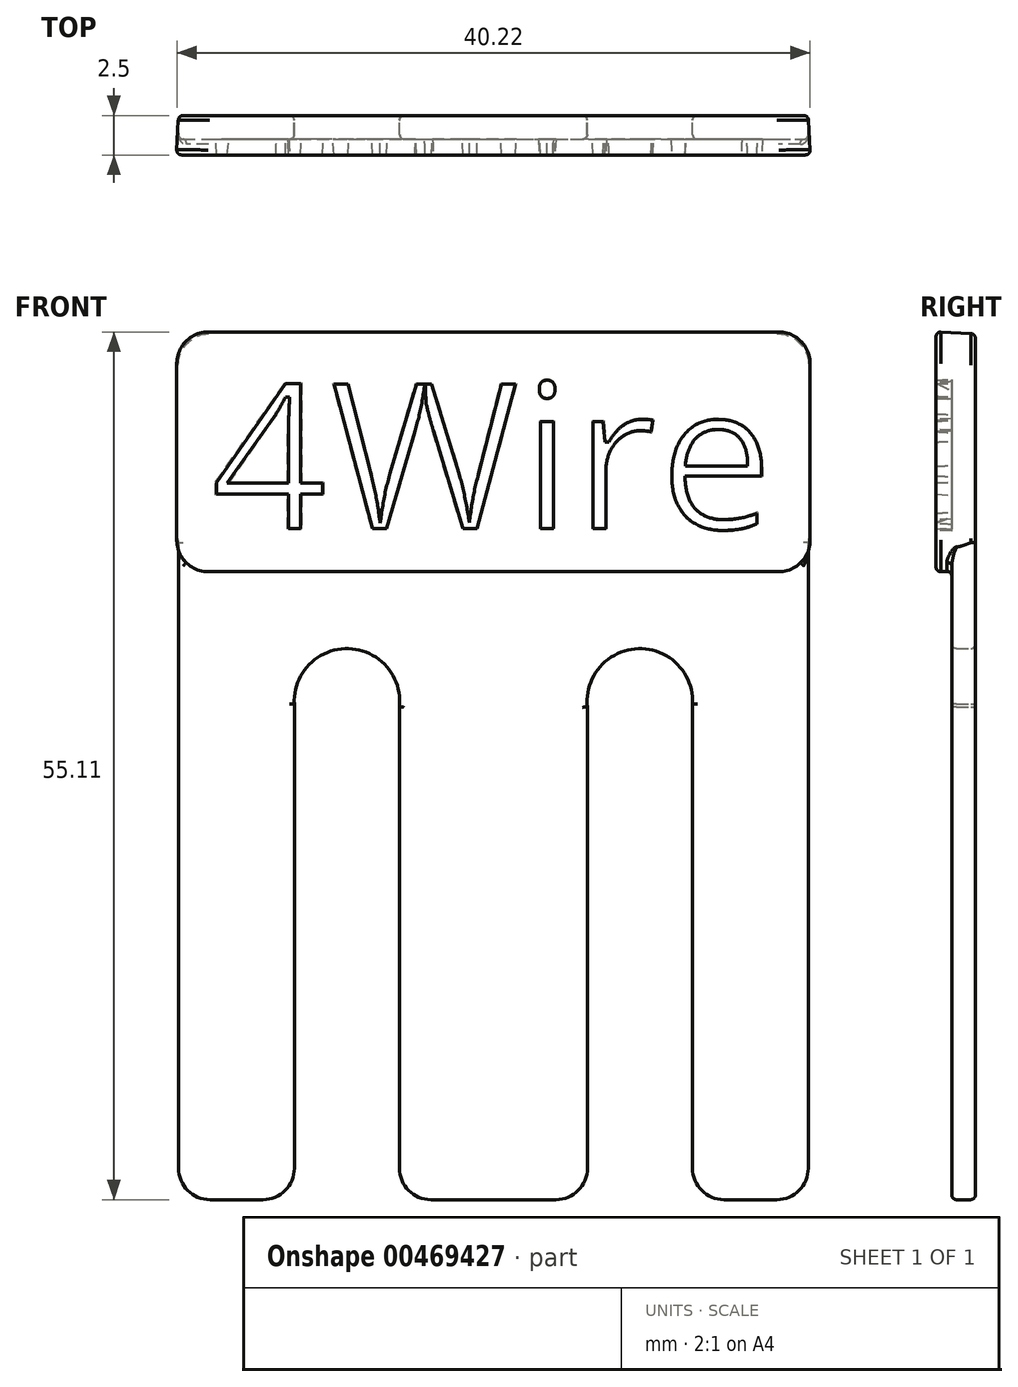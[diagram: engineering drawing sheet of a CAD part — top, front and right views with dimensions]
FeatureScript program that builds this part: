
annotation { "Feature Type Name" : "Feature", "Feature Type Description" : "" }
export const myFeature = defineFeature(function(context is Context, id is Id, definition is map)
    precondition{}
    {
        {
            var Q0;
            Q0=qCreatedBy(makeId("Front.planeOp"),FACE);
            var sketch = newSketch(context, id + "F0", { "sketchPlane" : qUnion([Q0])});
            skLineSegment(sketch, "E0.bottom", {"start": v(-20, 27.5) * mm, "end": v(20, 27.5) * mm});
            skLineSegment(sketch, "E0.top", {"start": v(-20, -27.5) * mm, "end": v(20, -27.5) * mm});
            skLineSegment(sketch, "E0.left", {"start": v(-20, 27.5) * mm, "end": v(-20, -27.5) * mm});
            skLineSegment(sketch, "E0.right", {"start": v(20, 27.5) * mm, "end": v(20, -27.5) * mm});
            skPoint(sketch, "E0.middle", {"position": v(0, 0) * mm});
            skLineSegment(sketch, "E1.top", {"start": v(-20, 12.5) * mm, "end": v(20, 12.5) * mm});
            skLineSegment(sketch, "E1.left", {"start": v(-20, 27.5) * mm, "end": v(-20, 12.5) * mm});
            skLineSegment(sketch, "E1.right", {"start": v(20, 27.5) * mm, "end": v(20, 12.5) * mm});
            skCircle(sketch, "E2", {"center": v(-9.3, 4.15) * mm, "radius": 3.35 * mm});
            skLineSegment(sketch, "E3", {"start": v(-12.65, 4.32) * mm, "end": v(-12.65, -27.5) * mm});
            skLineSegment(sketch, "E4", {"start": v(-5.97, 3.8) * mm, "end": v(-5.97, -27.5) * mm});
            skCircle(sketch, "E5.MirrorC", {"center": v(9.3, 4.15) * mm, "radius": 3.35 * mm});
            skLineSegment(sketch, "E6.MirrorCS", {"start": v(12.65, 4.32) * mm, "end": v(12.65, -27.5) * mm});
            skLineSegment(sketch, "E7.MirrorCS", {"start": v(5.97, 3.8) * mm, "end": v(5.97, -27.5) * mm});
            skText(sketch, "E8", { "text": "4Wire", "fontName": "OpenSans-Regular.ttf"});
            const initialGuessF0  = {"E8": [-0.018, 0.01501, 1, 0, 0.00949]};
            skSetInitialGuess(sketch, initialGuessF0);
            skSolve(sketch);
        }
        {
            var Q0;
            {var subQ5=sQuery(id+"F0.wireOp",EDGE,"E0.left");Q0=makeQuery(id+"F0.imprint","IMPRINT",FACE,{"disambiguationData":[TD([[makeQuery(id+"F0.imprint","IMPRINT",EDGE,{"derivedFrom":subQ5}),1.0]])]});}
            var Q1;
            Q1=makeQuery(id+"F0.imprint","IMPRINT",FACE,{"disambiguationData":[TD([[makeQuery(id+"F0.imprint","IMPRINT",EDGE,{"derivedFrom":sQuery(id+"F0.wireOp",EDGE,"E8.sketch_text.stroke-62")}),-1.0]])]});
            var Q2;
            Q2=makeQuery(id+"F0.imprint","IMPRINT",FACE,{"disambiguationData":[TD([[makeQuery(id+"F0.imprint","IMPRINT",EDGE,{"derivedFrom":sQuery(id+"F0.wireOp",EDGE,"E8.sketch_text.stroke-49")}),-1.0]])]});
            var Q3;
            Q3=makeQuery(id+"F0.imprint","IMPRINT",FACE,{"disambiguationData":[TD([[makeQuery(id+"F0.imprint","IMPRINT",EDGE,{"derivedFrom":sQuery(id+"F0.wireOp",EDGE,"E8.sketch_text.stroke-37")}),-1.0]])]});
            var Q4;
            Q4=makeQuery(id+"F0.imprint","IMPRINT",FACE,{"disambiguationData":[TD([[makeQuery(id+"F0.imprint","IMPRINT",EDGE,{"derivedFrom":sQuery(id+"F0.wireOp",EDGE,"E8.sketch_text.stroke-41")}),-1.0]])]});
            var Q5;
            Q5=makeQuery(id+"F0.imprint","IMPRINT",FACE,{"disambiguationData":[TD([[makeQuery(id+"F0.imprint","IMPRINT",EDGE,{"derivedFrom":sQuery(id+"F0.wireOp",EDGE,"E8.sketch_text.stroke-17")}),-1.0]])]});
            var Q6;
            Q6=makeQuery(id+"F0.imprint","IMPRINT",FACE,{"disambiguationData":[TD([[makeQuery(id+"F0.imprint","IMPRINT",EDGE,{"derivedFrom":sQuery(id+"F0.wireOp",EDGE,"E8.sketch_text.stroke-0")}),-1.0]])]});
            extrude(context, id + "F1", {"entities" : qUnion([Q0, Q1, Q2, Q3, Q4, Q5, Q6]), "depth" : 1.5 * mm});
        }
        {
            var Q0;
            Q0=makeQuery(id+"F0.imprint","IMPRINT",FACE,{"disambiguationData":[TD([[makeQuery(id+"F0.imprint","IMPRINT",EDGE,{"derivedFrom":sQuery(id+"F0.wireOp",EDGE,"E0.bottom")}),-1.0]])]});
            var Q1;
            Q1=makeQuery(id+"F0.imprint","IMPRINT",FACE,{"disambiguationData":[TD([[makeQuery(id+"F0.imprint","IMPRINT",EDGE,{"derivedFrom":sQuery(id+"F0.wireOp",EDGE,"E8.sketch_text.stroke-11")}),1.0]])]});
            var Q2;
            Q2=makeQuery(id+"F0.imprint","IMPRINT",FACE,{"disambiguationData":[TD([[makeQuery(id+"F0.imprint","IMPRINT",EDGE,{"derivedFrom":sQuery(id+"F0.wireOp",EDGE,"E8.sketch_text.stroke-76")}),1.0]])]});
            extrude(context, id + "F2", {"entities" : qUnion([Q0, Q1, Q2]), "operationType" : NewBodyOperationType.ADD, "depth" : 2.5 * mm, "hasDraft" : true, "draftAngle" : 3 * degree});
        }
        {
            var Q0;
            Q0=makeQuery(id+"F2.opExtrude","SWEPT_EDGE",EDGE,{"disambiguationData":[OSD([sQuery(id+"F0.wireOp",EDGE,"E0.bottom"),sQuery(id+"F0.wireOp",EDGE,"E1.right")])]});
            var Q1;
            Q1=makeQuery(id+"F2.opExtrude","SWEPT_EDGE",EDGE,{"disambiguationData":[OSD([sQuery(id+"F0.wireOp",EDGE,"E0.bottom"),sQuery(id+"F0.wireOp",EDGE,"E1.left")])]});
            var Q2;
            Q2=makeQuery(id+"F1.opExtrude","SWEPT_EDGE",EDGE,{"disambiguationData":[OSD([sQuery(id+"F0.wireOp",EDGE,"E0.top"),sQuery(id+"F0.wireOp",EDGE,"E3")])]});
            var Q3;
            Q3=makeQuery(id+"F1.opExtrude","SWEPT_EDGE",EDGE,{"disambiguationData":[OSD([sQuery(id+"F0.wireOp",EDGE,"E0.top"),sQuery(id+"F0.wireOp",EDGE,"E4")])]});
            var Q4;
            Q4=makeQuery(id+"F1.opExtrude","SWEPT_EDGE",EDGE,{"disambiguationData":[OSD([sQuery(id+"F0.wireOp",EDGE,"E0.top"),sQuery(id+"F0.wireOp",EDGE,"E7.MirrorCS")])]});
            var Q5;
            Q5=makeQuery(id+"F1.opExtrude","SWEPT_EDGE",EDGE,{"disambiguationData":[OSD([sQuery(id+"F0.wireOp",EDGE,"E0.top"),sQuery(id+"F0.wireOp",EDGE,"E6.MirrorCS")])]});
            var Q6;
            Q6=makeQuery(id+"F1.opExtrude","SWEPT_EDGE",EDGE,{"disambiguationData":[OSD([sQuery(id+"F0.wireOp",EDGE,"E0.top"),sQuery(id+"F0.wireOp",EDGE,"E0.right")])]});
            var Q7;
            Q7=makeQuery(id+"F1.opExtrude","SWEPT_EDGE",EDGE,{"disambiguationData":[OSD([sQuery(id+"F0.wireOp",EDGE,"E0.top"),sQuery(id+"F0.wireOp",EDGE,"E0.left")])]});
            var Q8;
            Q8=makeQuery(id+"F2.opExtrude","SWEPT_EDGE",EDGE,{"disambiguationData":[OSD([sQuery(id+"F0.wireOp",EDGE,"E0.right"),sQuery(id+"F0.wireOp",EDGE,"E1.top"),sQuery(id+"F0.wireOp",EDGE,"E1.right")])]});
            var Q9;
            Q9=makeQuery(id+"F2.opExtrude","SWEPT_EDGE",EDGE,{"disambiguationData":[OSD([sQuery(id+"F0.wireOp",EDGE,"E0.left"),sQuery(id+"F0.wireOp",EDGE,"E1.top"),sQuery(id+"F0.wireOp",EDGE,"E1.left")])]});
            fillet(context, id + "F3", {"entities" : qUnion([Q0, Q1, Q2, Q3, Q4, Q5, Q6, Q7, Q8, Q9]), "radius" : 2 * mm, "tangentPropagation" : true, "allowEdgeOverflow" : false});
        }
        {
            var Q0;
            Q0=makeQuery(id+"F2.opExtrude","CAP_EDGE",EDGE,{"disambiguationData":[OSD([sQuery(id+"F0.wireOp",EDGE,"E1.top")])],"isStart":false});
            var Q1;
            Q1=makeQuery(id+"F1.opExtrude","CAP_FACE",FACE,{"disambiguationData":[OSD([sQuery(id+"F0.wireOp",EDGE,"E0.top"),sQuery(id+"F0.wireOp",EDGE,"E0.left"),sQuery(id+"F0.wireOp",EDGE,"E0.right"),sQuery(id+"F0.wireOp",EDGE,"E1.top"),sQuery(id+"F0.wireOp",EDGE,"E2"),sQuery(id+"F0.wireOp",EDGE,"E3"),sQuery(id+"F0.wireOp",EDGE,"E4"),sQuery(id+"F0.wireOp",EDGE,"E5.MirrorC"),sQuery(id+"F0.wireOp",EDGE,"E6.MirrorCS"),sQuery(id+"F0.wireOp",EDGE,"E7.MirrorCS")])],"isStart":false});
            var Q2;
            {var subQ0=sQuery(id+"F0.wireOp",EDGE,"E8.sketch_text.stroke-80");var subQ1=sQuery(id+"F0.wireOp",EDGE,"E8.sketch_text.stroke-79");var subQ2=sQuery(id+"F0.wireOp",EDGE,"E8.sketch_text.stroke-78");var subQ3=sQuery(id+"F0.wireOp",EDGE,"E8.sketch_text.stroke-77");var subQ4=sQuery(id+"F0.wireOp",EDGE,"E8.sketch_text.stroke-76");var subQ5=sQuery(id+"F0.wireOp",EDGE,"E8.sketch_text.stroke-16");var subQ6=sQuery(id+"F0.wireOp",EDGE,"E8.sketch_text.stroke-15");var subQ7=sQuery(id+"F0.wireOp",EDGE,"E8.sketch_text.stroke-14");var subQ8=sQuery(id+"F0.wireOp",EDGE,"E8.sketch_text.stroke-13");var subQ9=sQuery(id+"F0.wireOp",EDGE,"E8.sketch_text.stroke-12");var subQ10=sQuery(id+"F0.wireOp",EDGE,"E8.sketch_text.stroke-11");var subQ11=sQuery(id+"F0.wireOp",EDGE,"E8.sketch_text.stroke-75");var subQ12=sQuery(id+"F0.wireOp",EDGE,"E8.sketch_text.stroke-74");var subQ13=sQuery(id+"F0.wireOp",EDGE,"E8.sketch_text.stroke-73");var subQ14=sQuery(id+"F0.wireOp",EDGE,"E8.sketch_text.stroke-72");var subQ15=sQuery(id+"F0.wireOp",EDGE,"E8.sketch_text.stroke-71");var subQ16=sQuery(id+"F0.wireOp",EDGE,"E8.sketch_text.stroke-70");var subQ17=sQuery(id+"F0.wireOp",EDGE,"E8.sketch_text.stroke-69");var subQ18=sQuery(id+"F0.wireOp",EDGE,"E8.sketch_text.stroke-68");var subQ19=sQuery(id+"F0.wireOp",EDGE,"E8.sketch_text.stroke-67");var subQ20=sQuery(id+"F0.wireOp",EDGE,"E8.sketch_text.stroke-66");var subQ21=sQuery(id+"F0.wireOp",EDGE,"E8.sketch_text.stroke-65");var subQ22=sQuery(id+"F0.wireOp",EDGE,"E8.sketch_text.stroke-64");var subQ23=sQuery(id+"F0.wireOp",EDGE,"E8.sketch_text.stroke-63");var subQ24=sQuery(id+"F0.wireOp",EDGE,"E8.sketch_text.stroke-62");var subQ25=sQuery(id+"F0.wireOp",EDGE,"E8.sketch_text.stroke-61");var subQ26=sQuery(id+"F0.wireOp",EDGE,"E8.sketch_text.stroke-60");var subQ27=sQuery(id+"F0.wireOp",EDGE,"E8.sketch_text.stroke-59");var subQ28=sQuery(id+"F0.wireOp",EDGE,"E8.sketch_text.stroke-58");var subQ29=sQuery(id+"F0.wireOp",EDGE,"E8.sketch_text.stroke-57");var subQ30=sQuery(id+"F0.wireOp",EDGE,"E8.sketch_text.stroke-56");var subQ31=sQuery(id+"F0.wireOp",EDGE,"E8.sketch_text.stroke-55");var subQ32=sQuery(id+"F0.wireOp",EDGE,"E8.sketch_text.stroke-54");var subQ33=sQuery(id+"F0.wireOp",EDGE,"E8.sketch_text.stroke-53");var subQ34=sQuery(id+"F0.wireOp",EDGE,"E8.sketch_text.stroke-52");var subQ35=sQuery(id+"F0.wireOp",EDGE,"E8.sketch_text.stroke-51");var subQ36=sQuery(id+"F0.wireOp",EDGE,"E8.sketch_text.stroke-50");var subQ37=sQuery(id+"F0.wireOp",EDGE,"E8.sketch_text.stroke-49");var subQ38=sQuery(id+"F0.wireOp",EDGE,"E8.sketch_text.stroke-48");var subQ39=sQuery(id+"F0.wireOp",EDGE,"E8.sketch_text.stroke-47");var subQ40=sQuery(id+"F0.wireOp",EDGE,"E8.sketch_text.stroke-46");var subQ41=sQuery(id+"F0.wireOp",EDGE,"E8.sketch_text.stroke-45");var subQ42=sQuery(id+"F0.wireOp",EDGE,"E8.sketch_text.stroke-44");var subQ43=sQuery(id+"F0.wireOp",EDGE,"E8.sketch_text.stroke-43");var subQ44=sQuery(id+"F0.wireOp",EDGE,"E8.sketch_text.stroke-42");var subQ45=sQuery(id+"F0.wireOp",EDGE,"E8.sketch_text.stroke-41");var subQ46=sQuery(id+"F0.wireOp",EDGE,"E8.sketch_text.stroke-40");var subQ47=sQuery(id+"F0.wireOp",EDGE,"E8.sketch_text.stroke-39");var subQ48=sQuery(id+"F0.wireOp",EDGE,"E8.sketch_text.stroke-38");var subQ49=sQuery(id+"F0.wireOp",EDGE,"E8.sketch_text.stroke-37");var subQ50=sQuery(id+"F0.wireOp",EDGE,"E8.sketch_text.stroke-36");var subQ51=sQuery(id+"F0.wireOp",EDGE,"E8.sketch_text.stroke-35");var subQ52=sQuery(id+"F0.wireOp",EDGE,"E8.sketch_text.stroke-34");var subQ53=sQuery(id+"F0.wireOp",EDGE,"E8.sketch_text.stroke-33");var subQ54=sQuery(id+"F0.wireOp",EDGE,"E8.sketch_text.stroke-32");var subQ55=sQuery(id+"F0.wireOp",EDGE,"E8.sketch_text.stroke-31");var subQ56=sQuery(id+"F0.wireOp",EDGE,"E8.sketch_text.stroke-30");var subQ57=sQuery(id+"F0.wireOp",EDGE,"E8.sketch_text.stroke-29");var subQ58=sQuery(id+"F0.wireOp",EDGE,"E8.sketch_text.stroke-28");var subQ59=sQuery(id+"F0.wireOp",EDGE,"E8.sketch_text.stroke-27");var subQ60=sQuery(id+"F0.wireOp",EDGE,"E8.sketch_text.stroke-26");var subQ61=sQuery(id+"F0.wireOp",EDGE,"E8.sketch_text.stroke-25");var subQ62=sQuery(id+"F0.wireOp",EDGE,"E8.sketch_text.stroke-24");var subQ63=sQuery(id+"F0.wireOp",EDGE,"E8.sketch_text.stroke-23");var subQ64=sQuery(id+"F0.wireOp",EDGE,"E8.sketch_text.stroke-22");var subQ65=sQuery(id+"F0.wireOp",EDGE,"E8.sketch_text.stroke-21");var subQ66=sQuery(id+"F0.wireOp",EDGE,"E8.sketch_text.stroke-20");var subQ67=sQuery(id+"F0.wireOp",EDGE,"E8.sketch_text.stroke-19");var subQ68=sQuery(id+"F0.wireOp",EDGE,"E8.sketch_text.stroke-18");var subQ69=sQuery(id+"F0.wireOp",EDGE,"E8.sketch_text.stroke-17");var subQ70=sQuery(id+"F0.wireOp",EDGE,"E8.sketch_text.stroke-10");var subQ71=sQuery(id+"F0.wireOp",EDGE,"E8.sketch_text.stroke-9");var subQ72=sQuery(id+"F0.wireOp",EDGE,"E8.sketch_text.stroke-8");var subQ73=sQuery(id+"F0.wireOp",EDGE,"E8.sketch_text.stroke-7");var subQ74=sQuery(id+"F0.wireOp",EDGE,"E8.sketch_text.stroke-6");var subQ75=sQuery(id+"F0.wireOp",EDGE,"E8.sketch_text.stroke-5");var subQ76=sQuery(id+"F0.wireOp",EDGE,"E8.sketch_text.stroke-4");var subQ77=sQuery(id+"F0.wireOp",EDGE,"E8.sketch_text.stroke-3");var subQ78=sQuery(id+"F0.wireOp",EDGE,"E8.sketch_text.stroke-2");var subQ79=sQuery(id+"F0.wireOp",EDGE,"E8.sketch_text.stroke-1");var subQ80=sQuery(id+"F0.wireOp",EDGE,"E8.sketch_text.stroke-0");var subQ81=sQuery(id+"F0.wireOp",EDGE,"E1.top");Q2=makeQuery(id+"F2.boolean.opBoolean","MERGE",FACE,{"derivedFrom":[makeQuery(id+"F1.opExtrude","CAP_FACE",FACE,{"disambiguationData":[OSD([sQuery(id+"F0.wireOp",EDGE,"E0.top"),sQuery(id+"F0.wireOp",EDGE,"E0.left"),sQuery(id+"F0.wireOp",EDGE,"E0.right"),subQ81,sQuery(id+"F0.wireOp",EDGE,"E2"),sQuery(id+"F0.wireOp",EDGE,"E3"),sQuery(id+"F0.wireOp",EDGE,"E4"),sQuery(id+"F0.wireOp",EDGE,"E5.MirrorC"),sQuery(id+"F0.wireOp",EDGE,"E6.MirrorCS"),sQuery(id+"F0.wireOp",EDGE,"E7.MirrorCS")])],"isStart":true}),makeQuery(id+"F1.opExtrude","CAP_FACE",FACE,{"disambiguationData":[OSD([subQ80,subQ79,subQ78,subQ77,subQ76,subQ75,subQ74,subQ73,subQ72,subQ71,subQ70,subQ10,subQ9,subQ8,subQ7,subQ6,subQ5])],"isStart":true}),makeQuery(id+"F1.opExtrude","CAP_FACE",FACE,{"disambiguationData":[OSD([subQ69,subQ68,subQ67,subQ66,subQ65,subQ64,subQ63,subQ62,subQ61,subQ60,subQ59,subQ58,subQ57,subQ56,subQ55,subQ54,subQ53,subQ52,subQ51,subQ50])],"isStart":true}),makeQuery(id+"F1.opExtrude","CAP_FACE",FACE,{"disambiguationData":[OSD([subQ49,subQ48,subQ47,subQ46])],"isStart":true}),makeQuery(id+"F1.opExtrude","CAP_FACE",FACE,{"disambiguationData":[OSD([subQ45,subQ44,subQ43,subQ42,subQ41,subQ40,subQ39,subQ38])],"isStart":true}),makeQuery(id+"F1.opExtrude","CAP_FACE",FACE,{"disambiguationData":[OSD([subQ37,subQ36,subQ35,subQ34,subQ33,subQ32,subQ31,subQ30,subQ29,subQ28,subQ27,subQ26,subQ25])],"isStart":true}),makeQuery(id+"F1.opExtrude","CAP_FACE",FACE,{"disambiguationData":[OSD([subQ24,subQ23,subQ22,subQ21,subQ20,subQ19,subQ18,subQ17,subQ16,subQ15,subQ14,subQ13,subQ12,subQ11,subQ4,subQ3,subQ2,subQ1,subQ0])],"isStart":true}),makeQuery(id+"F2.opExtrude","CAP_FACE",FACE,{"disambiguationData":[OSD([sQuery(id+"F0.wireOp",EDGE,"E0.bottom"),subQ81,sQuery(id+"F0.wireOp",EDGE,"E1.left"),sQuery(id+"F0.wireOp",EDGE,"E1.right"),subQ80,subQ79,subQ78,subQ77,subQ76,subQ75,subQ74,subQ73,subQ72,subQ71,subQ70,subQ69,subQ68,subQ67,subQ66,subQ65,subQ64,subQ63,subQ62,subQ61,subQ60,subQ59,subQ58,subQ57,subQ56,subQ55,subQ54,subQ53,subQ52,subQ51,subQ50,subQ49,subQ48,subQ47,subQ46,subQ45,subQ44,subQ43,subQ42,subQ41,subQ40,subQ39,subQ38,subQ37,subQ36,subQ35,subQ34,subQ33,subQ32,subQ31,subQ30,subQ29,subQ28,subQ27,subQ26,subQ25,subQ24,subQ23,subQ22,subQ21,subQ20,subQ19,subQ18,subQ17,subQ16,subQ15,subQ14,subQ13,subQ12,subQ11])],"isStart":true}),makeQuery(id+"F2.opExtrude","CAP_FACE",FACE,{"disambiguationData":[OSD([subQ10,subQ9,subQ8,subQ7,subQ6,subQ5])],"isStart":true}),makeQuery(id+"F2.opExtrude","CAP_FACE",FACE,{"disambiguationData":[OSD([subQ4,subQ3,subQ2,subQ1,subQ0])],"isStart":true})]});}
            fillet(context, id + "F4", {"entities" : qUnion([Q0, Q1, Q2]), "radius" : 0.3 * mm, "tangentPropagation" : true, "allowEdgeOverflow" : false});
        }
    });
